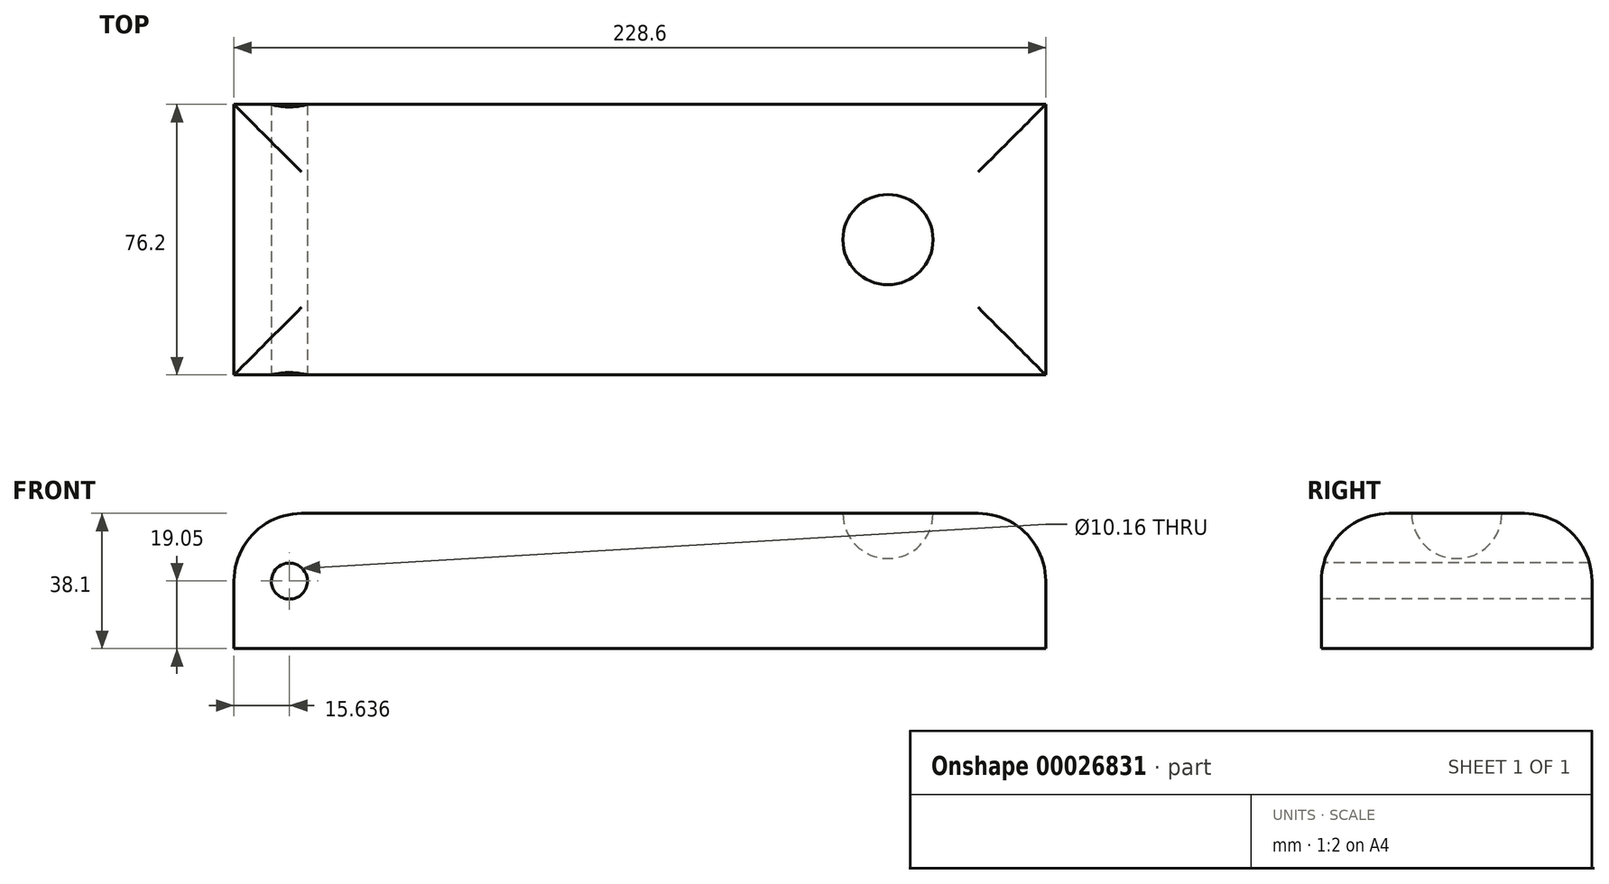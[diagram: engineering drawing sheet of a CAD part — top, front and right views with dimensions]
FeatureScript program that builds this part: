
annotation { "Feature Type Name" : "Feature", "Feature Type Description" : "" }
export const myFeature = defineFeature(function(context is Context, id is Id, definition is map)
    precondition{}
    {
        {
            var Q0;
            Q0=qCreatedBy(makeId("Top.planeOp"),FACE);
            var sketch = newSketch(context, id + "F0", { "sketchPlane" : qUnion([Q0])});
            skLineSegment(sketch, "E0.rect.bottom", {"start": v(-114.3, 38.1) * mm, "end": v(114.3, 38.1) * mm});
            skLineSegment(sketch, "E0.rect.top", {"start": v(-114.3, -38.1) * mm, "end": v(114.3, -38.1) * mm});
            skLineSegment(sketch, "E0.rect.left", {"start": v(-114.3, 38.1) * mm, "end": v(-114.3, -38.1) * mm});
            skLineSegment(sketch, "E0.rect.right", {"start": v(114.3, 38.1) * mm, "end": v(114.3, -38.1) * mm});
            skPoint(sketch, "E0.rect.middle", {"position": v(0, 0) * mm});
            skSolve(sketch);
        }
        {
            var Q0;
            Q0=makeQuery(id+"F0.imprint","IMPRINT",FACE,{"disambiguationData":[TD([[makeQuery(id+"F0.imprint","IMPRINT",EDGE,{"derivedFrom":sQuery(id+"F0.wireOp",EDGE,"E0.rect.bottom")}),-1.0]])]});
            var Q1;
            Q1=makeQuery(id+"F0.imprint","IMPRINT",FACE,{"disambiguationData":[TD([[makeQuery(id+"F0.imprint","IMPRINT",EDGE,{"derivedFrom":sQuery(id+"F0.wireOp",EDGE,"1a045472-f1f8-4227-9877-c0e6ea73bdda")}),1.0]])]});
            extrude(context, id + "F1", {"entities" : qUnion([Q0, Q1]), "depth" : 38.1 * mm});
        }
        {
            var Q0;
            Q0=makeQuery(id+"F1.opExtrude","CAP_FACE",FACE,{"disambiguationData":[OSD([sQuery(id+"F0.wireOp",EDGE,"E0.rect.bottom"),sQuery(id+"F0.wireOp",EDGE,"E0.rect.top"),sQuery(id+"F0.wireOp",EDGE,"E0.rect.left"),sQuery(id+"F0.wireOp",EDGE,"E0.rect.right")])],"isStart":false});
            var sketch = newSketch(context, id + "F2", { "sketchPlane" : qUnion([Q0])});
            skArc(sketch, "E1", {"start": v(69.85, -12.7) * mm, "mid": v(82.55, 0) * mm, "end": v(69.85, 12.7) * mm});
            skLineSegment(sketch, "E2", {"start": v(69.85, 12.7) * mm, "end": v(69.85, -12.7) * mm});
            skSolve(sketch);
        }
        {
            var Q0;
            Q0=makeQuery(id+"F2.imprint","IMPRINT",FACE,{"disambiguationData":[TD([[makeQuery(id+"F2.imprint","IMPRINT",EDGE,{"derivedFrom":sQuery(id+"F2.wireOp",EDGE,"E1")}),1.0]])]});
            var Q1;
            Q1=sQuery(id+"F2.wireOp",EDGE,"E2");
            revolve(context, id + "F3", {"operationType" : NewBodyOperationType.REMOVE, "entities" : qUnion([Q0]), "axis" : qUnion([Q1]), "revolveType" : RevolveType.FULL, "oppositeDirection" : true});
        }
        {
            var Q0;
            Q0=makeQuery(id+"F1.opExtrude","SWEPT_FACE",FACE,{"disambiguationData":[OSD([sQuery(id+"F0.wireOp",EDGE,"E0.rect.top")])]});
            var sketch = newSketch(context, id + "F4", { "sketchPlane" : qUnion([Q0])});
            skCircle(sketch, "E3", {"center": v(-98.66, 19.05) * mm, "radius": 5.08 * mm});
            skSolve(sketch);
        }
        {
            var Q0;
            Q0=makeQuery(id+"F4.imprint","IMPRINT",FACE,{"disambiguationData":[TD([[makeQuery(id+"F4.imprint","IMPRINT",EDGE,{"derivedFrom":sQuery(id+"F4.wireOp",EDGE,"E3")}),1.0]])]});
            extrude(context, id + "F5", {"entities" : qUnion([Q0]), "operationType" : NewBodyOperationType.REMOVE, "oppositeDirection" : true, "depth" : 76.2 * mm});
        }
        {
            var Q0;
            Q0=makeQuery(id+"F1.opExtrude","CAP_EDGE",EDGE,{"disambiguationData":[OSD([sQuery(id+"F0.wireOp",EDGE,"E0.rect.top")])],"isStart":false});
            var Q1;
            Q1=makeQuery(id+"F1.opExtrude","CAP_EDGE",EDGE,{"disambiguationData":[OSD([sQuery(id+"F0.wireOp",EDGE,"E0.rect.right")])],"isStart":false});
            var Q2;
            Q2=makeQuery(id+"F1.opExtrude","CAP_EDGE",EDGE,{"disambiguationData":[OSD([sQuery(id+"F0.wireOp",EDGE,"E0.rect.bottom")])],"isStart":false});
            var Q3;
            Q3=makeQuery(id+"F1.opExtrude","CAP_EDGE",EDGE,{"disambiguationData":[OSD([sQuery(id+"F0.wireOp",EDGE,"E0.rect.left")])],"isStart":false});
            fillet(context, id + "F6", {"entities" : qUnion([Q0, Q1, Q2, Q3]), "radius" : 19.05 * mm, "tangentPropagation" : true, "allowEdgeOverflow" : false});
        }
    });
